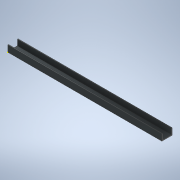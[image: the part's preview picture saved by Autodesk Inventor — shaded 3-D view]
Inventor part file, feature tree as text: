
AUTODESK INVENTOR PART (.ipt)
format: ipt  version: 2020 (Build 240168000, 168)  size: 110,592 bytes
history: native  units: mm
features: sketch x2, extrude x1
ambient origin geometry x8: Origin, YZ Plane, XZ Plane, XY Plane, X Axis, Y Axis, Z Axis, Center Point
bodies: Solid1 (feature_tree)
feature tree (3):
  sketch  "Sketch1"  dims[d0=22.5mm d1=14.0mm]
  extrude  "Extrusion1"  Depth=14.0mm
  sketch  "Sketch2"  dims[d2=14.0mm d3=1.588mm d4=12.412mm d5=19.324mm d6=334.01mm d7=0.0mm]
